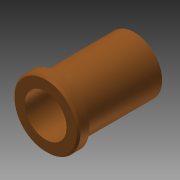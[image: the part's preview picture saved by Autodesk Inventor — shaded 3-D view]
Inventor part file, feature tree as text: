
AUTODESK INVENTOR PART (.ipt)
format: ipt  version: 2014 SP1 (Build 180222100, 222)  size: 97,280 bytes
history: native  units: in
note: dims shown in document units (in); Inventor stores cm internally (conversion verified against a paired STEP export)
features: extrude x2, sketch x1, chamfer x1
ambient origin geometry x8: Origin, YZ Plane, XZ Plane, XY Plane, X Axis, Y Axis, Z Axis, Center Point
bodies: Solid1 (feature_tree)
feature tree (4):
  sketch  "Sketch1"  dims[d0=0.372in d1=0.2362in d2=0.061in d3=0.0in d4=0.315in d5=0.4398in d6=0.0in d7=0.0098in d8=0.0787in d9=45.0deg]
  extrude  "Extrusion1"  Depth=0.4398in
  extrude  "Extrusion2"  Depth=0.061in TaperAngle=0.0deg
  chamfer  "Chamfer1"  Distance=0.315in
